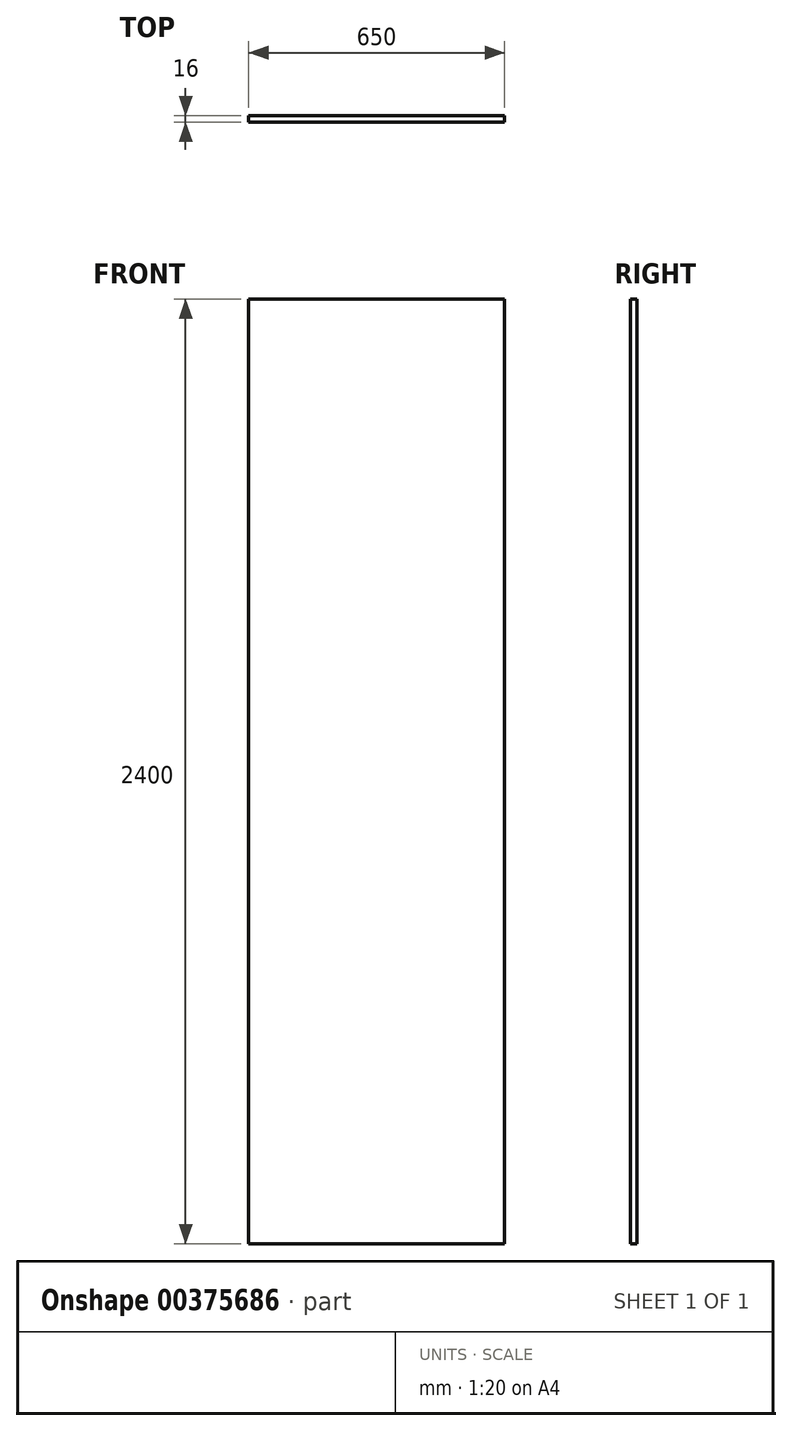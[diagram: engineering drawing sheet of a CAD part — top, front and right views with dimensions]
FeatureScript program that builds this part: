
annotation { "Feature Type Name" : "Feature", "Feature Type Description" : "" }
export const myFeature = defineFeature(function(context is Context, id is Id, definition is map)
    precondition{}
    {
        {
            var Q0;
            Q0=qCreatedBy(makeId("Front.planeOp"),FACE);
            var sketch = newSketch(context, id + "F0", { "sketchPlane" : qUnion([Q0])});
            skLineSegment(sketch, "E0.bottom", {"start": v(-335.85, 2025.51) * mm, "end": v(314.15, 2025.51) * mm});
            skLineSegment(sketch, "E0.top", {"start": v(-335.85, -374.49) * mm, "end": v(314.15, -374.49) * mm});
            skLineSegment(sketch, "E0.left", {"start": v(-335.85, 2025.51) * mm, "end": v(-335.85, -374.49) * mm});
            skLineSegment(sketch, "E0.right", {"start": v(314.15, 2025.51) * mm, "end": v(314.15, -374.49) * mm});
            skSolve(sketch);
        }
        {
            var Q0;
            Q0 = qSketchRegion(id + "F0", true);
            extrude(context, id + "F1", {"entities" : qUnion([Q0]), "depth" : 16 * mm});
        }
    });
